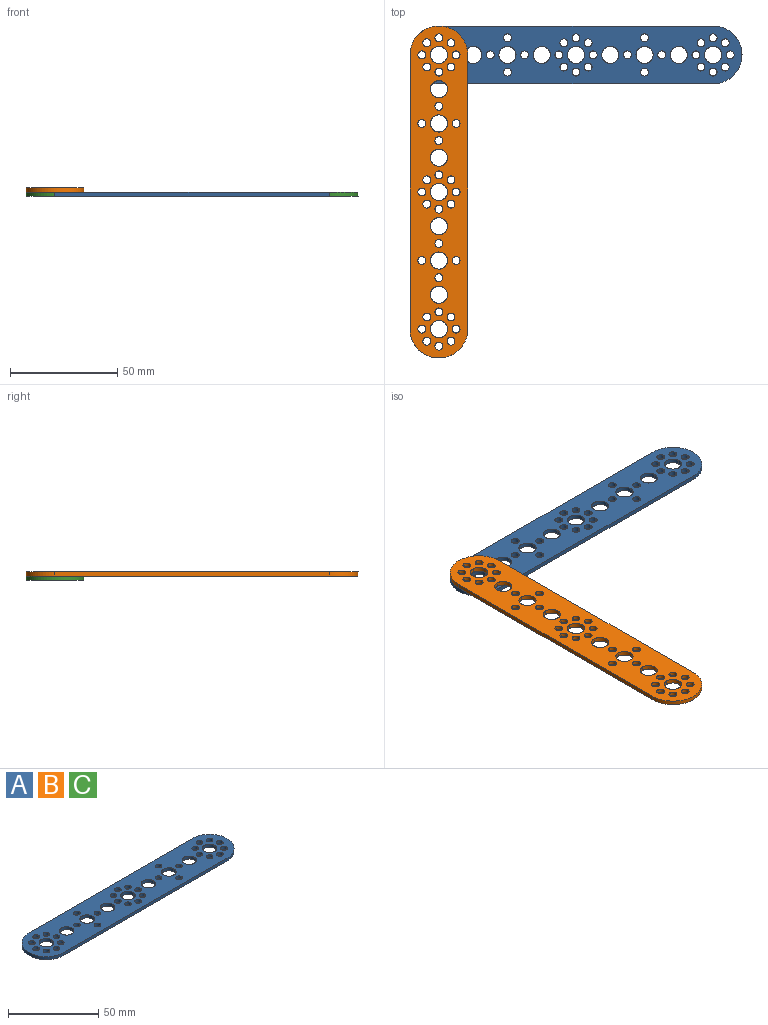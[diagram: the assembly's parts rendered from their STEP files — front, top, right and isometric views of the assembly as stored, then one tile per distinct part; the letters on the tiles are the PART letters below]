
ASSEMBLY  parts=3 mates=1
PART A: 88 faces, bbox 155.1x27.1x2.1 mm
  f0: plane 155.12x27.08mm, normal (0,0,-1), area 3232.1mm2, adj f1,f2,f3,f4,f5,f6,f7,f8
  f1: plane 128x2mm, normal (0,-1,0), area 256mm2, adj f0,f2,f4,f87
  f2: cylinder r=13.5mm len=27mm, axis (0,0,-1), area 84.8mm2, adj f0,f1,f3,f87
  f3: plane 128x2mm, normal (0,1,0), area 256mm2, adj f0,f2,f4,f87
  f4: cylinder r=13.5mm len=27mm, axis (0,0,-1), area 84.8mm2, adj f0,f1,f3,f87
  f5: cylinder r=1.85mm len=3.7mm, axis (0,0,-1), area 11.6mm2, adj f0,f6,f87
  f6: cylinder r=1.85mm len=3.7mm, axis (0,0,-1), area 11.6mm2, adj f0,f5,f87
  f7: cylinder r=1.85mm len=3.7mm, axis (0,0,-1), area 11.6mm2, adj f0,f8,f87
  f8: cylinder r=1.85mm len=3.7mm, axis (0,0,-1), area 11.6mm2, adj f0,f7,f87
  f9: cylinder r=1.85mm len=3.7mm, axis (0,0,-1), area 11.6mm2, adj f0,f10,f87
  f10: cylinder r=1.85mm len=3.7mm, axis (0,0,-1), area 11.6mm2, adj f0,f9,f87
  f11: cylinder r=1.85mm len=3.7mm, axis (0,0,-1), area 11.6mm2, adj f0,f12,f87
  f12: cylinder r=1.85mm len=3.7mm, axis (0,0,-1), area 11.6mm2, adj f0,f11,f87
  f13: cylinder r=4mm len=8mm, axis (0,0,-1), area 25.1mm2, adj f0,f14,f87
  f14: cylinder r=4mm len=8mm, axis (0,0,-1), area 25.1mm2, adj f0,f13,f87
  f15: cylinder r=1.85mm len=3.7mm, axis (0,0,-1), area 11.6mm2, adj f0,f16,f87
  f16: cylinder r=1.85mm len=3.7mm, axis (0,0,-1), area 11.6mm2, adj f0,f15,f87
  f17: cylinder r=1.85mm len=3.7mm, axis (0,0,-1), area 11.6mm2, adj f0,f18,f87
  f18: cylinder r=1.85mm len=3.7mm, axis (0,0,-1), area 11.6mm2, adj f0,f17,f87
  f19: cylinder r=1.85mm len=3.7mm, axis (0,0,-1), area 11.6mm2, adj f0,f20,f87
  f20: cylinder r=1.85mm len=3.7mm, axis (0,0,-1), area 11.6mm2, adj f0,f19,f87
  f21: cylinder r=1.85mm len=3.7mm, axis (0,0,-1), area 11.6mm2, adj f0,f22,f87
  f22: cylinder r=1.85mm len=3.7mm, axis (0,0,-1), area 11.6mm2, adj f0,f21,f87
  f23: cylinder r=1.85mm len=3.7mm, axis (0,0,-1), area 11.6mm2, adj f0,f24,f87
  f24: cylinder r=1.85mm len=3.7mm, axis (0,0,-1), area 11.6mm2, adj f0,f23,f87
  f25: cylinder r=1.85mm len=3.7mm, axis (0,0,-1), area 11.6mm2, adj f0,f26,f87
  f26: cylinder r=1.85mm len=3.7mm, axis (0,0,-1), area 11.6mm2, adj f0,f25,f87
  f27: cylinder r=1.85mm len=3.7mm, axis (0,0,-1), area 11.6mm2, adj f0,f28,f87
  f28: cylinder r=1.85mm len=3.7mm, axis (0,0,-1), area 11.6mm2, adj f0,f27,f87
  f29: cylinder r=4mm len=8mm, axis (0,0,-1), area 25.1mm2, adj f0,f30,f87
  f30: cylinder r=4mm len=8mm, axis (0,0,-1), area 25.1mm2, adj f0,f29,f87
  f31: cylinder r=1.85mm len=3.7mm, axis (0,0,-1), area 11.6mm2, adj f0,f32,f87
  f32: cylinder r=1.85mm len=3.7mm, axis (0,0,-1), area 11.6mm2, adj f0,f31,f87
  f33: cylinder r=1.85mm len=3.7mm, axis (0,0,-1), area 11.6mm2, adj f0,f34,f87
  f34: cylinder r=1.85mm len=3.7mm, axis (0,0,-1), area 11.6mm2, adj f0,f33,f87
  f35: cylinder r=1.85mm len=3.7mm, axis (0,0,-1), area 11.6mm2, adj f0,f36,f87
  f36: cylinder r=1.85mm len=3.7mm, axis (0,0,-1), area 11.6mm2, adj f0,f35,f87
  f37: cylinder r=1.85mm len=3.7mm, axis (0,0,-1), area 11.6mm2, adj f0,f38,f87
  f38: cylinder r=1.85mm len=3.7mm, axis (0,0,-1), area 11.6mm2, adj f0,f37,f87
  f39: cylinder r=1.85mm len=3.7mm, axis (0,0,-1), area 11.6mm2, adj f0,f40,f87
  f40: cylinder r=1.85mm len=3.7mm, axis (0,0,-1), area 11.6mm2, adj f0,f39,f87
  f41: cylinder r=1.85mm len=3.7mm, axis (0,0,-1), area 11.6mm2, adj f0,f42,f87
  f42: cylinder r=1.85mm len=3.7mm, axis (0,0,-1), area 11.6mm2, adj f0,f41,f87
  f43: cylinder r=4mm len=8mm, axis (0,0,-1), area 25.1mm2, adj f0,f44,f87
  f44: cylinder r=4mm len=8mm, axis (0,0,-1), area 25.1mm2, adj f0,f43,f87
  f45: cylinder r=4mm len=8mm, axis (0,0,-1), area 25.1mm2, adj f0,f46,f87
  f46: cylinder r=4mm len=8mm, axis (0,0,-1), area 25.1mm2, adj f0,f45,f87
  f47: cylinder r=1.85mm len=3.7mm, axis (0,0,-1), area 11.6mm2, adj f0,f48,f87
  f48: cylinder r=1.85mm len=3.7mm, axis (0,0,-1), area 11.6mm2, adj f0,f47,f87
  f49: cylinder r=1.85mm len=3.7mm, axis (0,0,-1), area 11.6mm2, adj f0,f50,f87
  f50: cylinder r=1.85mm len=3.7mm, axis (0,0,-1), area 11.6mm2, adj f0,f49,f87
  f51: cylinder r=1.85mm len=3.7mm, axis (0,0,-1), area 11.6mm2, adj f0,f52,f87
  f52: cylinder r=1.85mm len=3.7mm, axis (0,0,-1), area 11.6mm2, adj f0,f51,f87
  f53: cylinder r=1.85mm len=3.7mm, axis (0,0,-1), area 11.6mm2, adj f0,f54,f87
  f54: cylinder r=1.85mm len=3.7mm, axis (0,0,-1), area 11.6mm2, adj f0,f53,f87
  f55: cylinder r=1.85mm len=3.7mm, axis (0,0,-1), area 11.6mm2, adj f0,f56,f87
  f56: cylinder r=1.85mm len=3.7mm, axis (0,0,-1), area 11.6mm2, adj f0,f55,f87
  f57: cylinder r=1.85mm len=3.7mm, axis (0,0,-1), area 11.6mm2, adj f0,f58,f87
  f58: cylinder r=1.85mm len=3.7mm, axis (0,0,-1), area 11.6mm2, adj f0,f57,f87
  f59: cylinder r=4mm len=8mm, axis (0,0,-1), area 25.1mm2, adj f0,f60,f87
  f60: cylinder r=4mm len=8mm, axis (0,0,-1), area 25.1mm2, adj f0,f59,f87
  f61: cylinder r=4mm len=8mm, axis (0,0,-1), area 25.1mm2, adj f0,f62,f87
  f62: cylinder r=4mm len=8mm, axis (0,0,-1), area 25.1mm2, adj f0,f61,f87
  f63: cylinder r=1.85mm len=3.7mm, axis (0,0,-1), area 11.6mm2, adj f0,f64,f87
  f64: cylinder r=1.85mm len=3.7mm, axis (0,0,-1), area 11.6mm2, adj f0,f63,f87
  f65: cylinder r=1.85mm len=3.7mm, axis (0,0,-1), area 11.6mm2, adj f0,f66,f87
  f66: cylinder r=1.85mm len=3.7mm, axis (0,0,-1), area 11.6mm2, adj f0,f65,f87
  f67: cylinder r=1.85mm len=3.7mm, axis (0,0,-1), area 11.6mm2, adj f0,f68,f87
  f68: cylinder r=1.85mm len=3.7mm, axis (0,0,-1), area 11.6mm2, adj f0,f67,f87
  f69: cylinder r=1.85mm len=3.7mm, axis (0,0,-1), area 11.6mm2, adj f0,f70,f87
  f70: cylinder r=1.85mm len=3.7mm, axis (0,0,-1), area 11.6mm2, adj f0,f69,f87
  f71: cylinder r=4mm len=8mm, axis (0,0,-1), area 25.1mm2, adj f0,f72,f87
  f72: cylinder r=4mm len=8mm, axis (0,0,-1), area 25.1mm2, adj f0,f71,f87
  f73: cylinder r=1.85mm len=3.7mm, axis (0,0,-1), area 11.6mm2, adj f0,f74,f87
  f74: cylinder r=1.85mm len=3.7mm, axis (0,0,-1), area 11.6mm2, adj f0,f73,f87
  f75: cylinder r=4mm len=8mm, axis (0,0,-1), area 25.1mm2, adj f0,f76,f87
  f76: cylinder r=4mm len=8mm, axis (0,0,-1), area 25.1mm2, adj f0,f75,f87
  f77: cylinder r=4mm len=8mm, axis (0,0,-1), area 25.1mm2, adj f0,f78,f87
  f78: cylinder r=4mm len=8mm, axis (0,0,-1), area 25.1mm2, adj f0,f77,f87
  f79: cylinder r=1.85mm len=3.7mm, axis (0,0,-1), area 11.6mm2, adj f0,f80,f87
  f80: cylinder r=1.85mm len=3.7mm, axis (0,0,-1), area 11.6mm2, adj f0,f79,f87
  f81: cylinder r=1.85mm len=3.7mm, axis (0,0,-1), area 11.6mm2, adj f0,f82,f87
  f82: cylinder r=1.85mm len=3.7mm, axis (0,0,-1), area 11.6mm2, adj f0,f81,f87
  f83: cylinder r=1.85mm len=3.7mm, axis (0,0,-1), area 11.6mm2, adj f0,f84,f87
  f84: cylinder r=1.85mm len=3.7mm, axis (0,0,-1), area 11.6mm2, adj f0,f83,f87
  f85: cylinder r=1.85mm len=3.7mm, axis (0,0,-1), area 11.6mm2, adj f0,f86,f87
  f86: cylinder r=1.85mm len=3.7mm, axis (0,0,-1), area 11.6mm2, adj f0,f85,f87
  f87: plane 155.12x27.08mm, normal (0,0,1), area 3232.1mm2, adj f1,f2,f3,f4,f5,f6,f7,f8
PART B: same geometry as A
PART C: same geometry as A
PLACE A t=(2.52,10.43,12.45)mm
PLACE B rot(axis=(0.71,-0.71,0),180deg) t=(-61.48,-53.57,16.45)mm
PLACE C t=(2.52,10.43,12.45)mm
MATE fastened B.f4 <-> C.f4  axis (0,0,1) through (-61.48,10.43,14.45)mm
